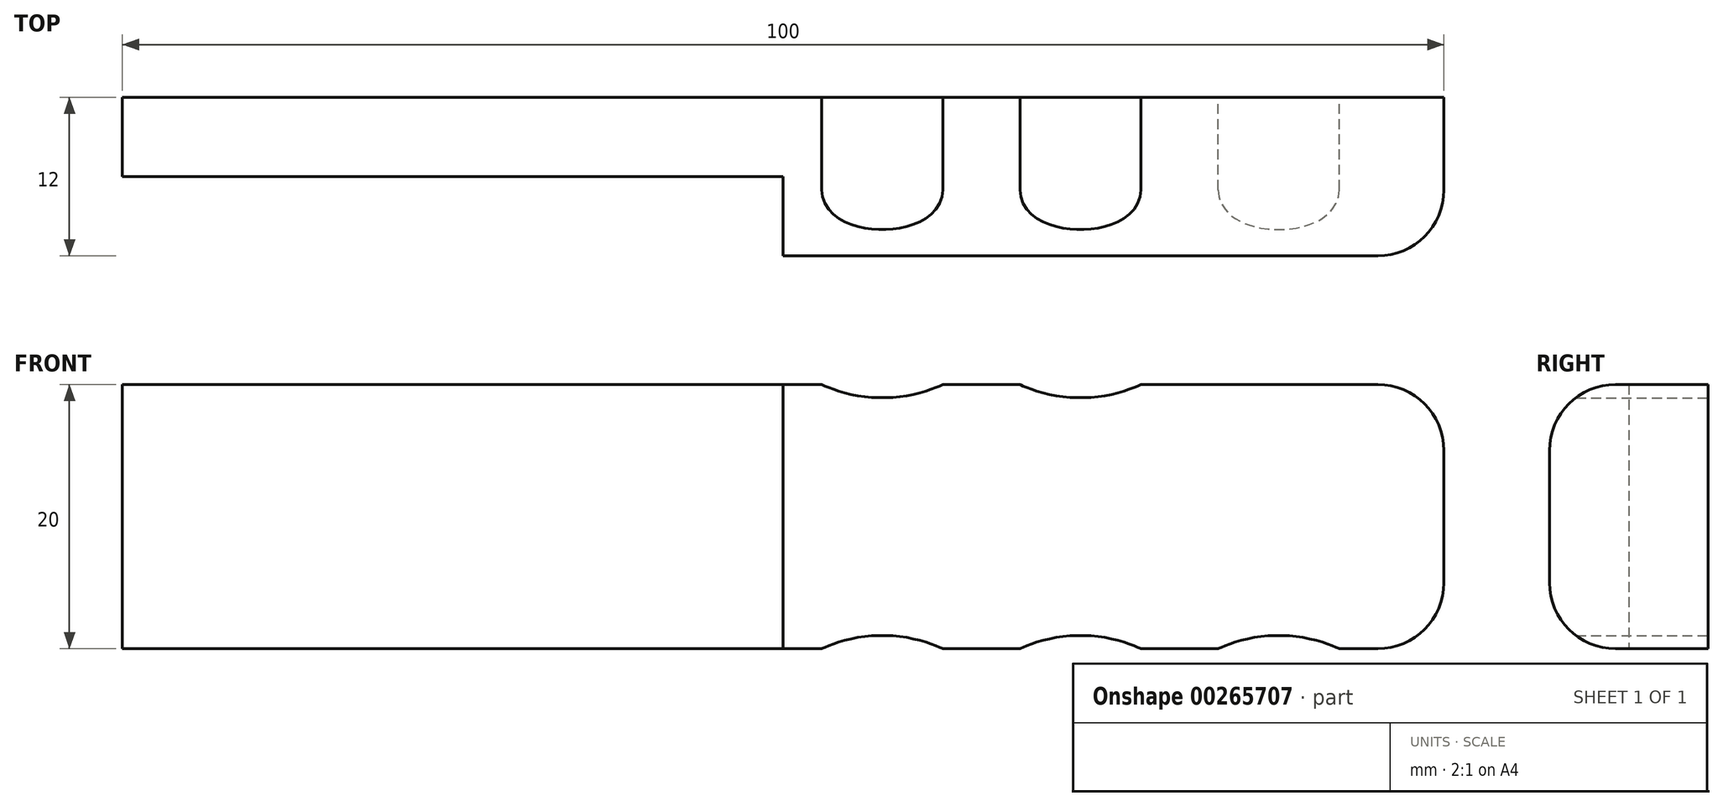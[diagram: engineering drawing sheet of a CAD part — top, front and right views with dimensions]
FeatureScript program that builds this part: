
annotation { "Feature Type Name" : "Feature", "Feature Type Description" : "" }
export const myFeature = defineFeature(function(context is Context, id is Id, definition is map)
    precondition{}
    {
        {
            var Q0;
            Q0=qCreatedBy(makeId("Front.planeOp"),FACE);
            var sketch = newSketch(context, id + "F0", { "sketchPlane" : qUnion([Q0])});
            skLineSegment(sketch, "E0.bottom", {"start": v(50, 10) * mm, "end": v(-50, 10) * mm});
            skLineSegment(sketch, "E0.top", {"start": v(50, -10) * mm, "end": v(-50, -10) * mm});
            skLineSegment(sketch, "E0.left", {"start": v(50, 10) * mm, "end": v(50, -10) * mm});
            skLineSegment(sketch, "E0.right", {"start": v(-50, 10) * mm, "end": v(-50, -10) * mm});
            skPoint(sketch, "E0.middle", {"position": v(0, 0) * mm});
            skSolve(sketch);
        }
        {
            var Q0;
            Q0=makeQuery(id+"F0.imprint","IMPRINT",FACE,{"disambiguationData":[TD([[makeQuery(id+"F0.imprint","IMPRINT",EDGE,{"derivedFrom":sQuery(id+"F0.wireOp",EDGE,"E0.bottom")}),1.0]])]});
            extrude(context, id + "F1", {"entities" : qUnion([Q0]), "depth" : 6 * mm});
        }
        {
            var Q0;
            Q0=makeQuery(id+"F1.opExtrude","SWEPT_EDGE",EDGE,{"disambiguationData":[OSD([sQuery(id+"F0.wireOp",EDGE,"E0.bottom"),sQuery(id+"F0.wireOp",EDGE,"E0.left")])]});
            var Q1;
            Q1=makeQuery(id+"F1.opExtrude","SWEPT_EDGE",EDGE,{"disambiguationData":[OSD([sQuery(id+"F0.wireOp",EDGE,"E0.top"),sQuery(id+"F0.wireOp",EDGE,"E0.left")])]});
            fillet(context, id + "F2", {"entities" : qUnion([Q0, Q1]), "radius" : 5 * mm, "tangentPropagation" : true, "allowEdgeOverflow" : false});
        }
        {
            var Q0;
            Q0=makeQuery(id+"F1.opExtrude","CAP_FACE",FACE,{"disambiguationData":[OSD([sQuery(id+"F0.wireOp",EDGE,"E0.bottom"),sQuery(id+"F0.wireOp",EDGE,"E0.top"),sQuery(id+"F0.wireOp",EDGE,"E0.left"),sQuery(id+"F0.wireOp",EDGE,"E0.right")])],"isStart":false});
            var sketch = newSketch(context, id + "F3", { "sketchPlane" : qUnion([Q0])});
            skLineSegment(sketch, "E1", {"start": v(0, 10) * mm, "end": v(0, -10) * mm});
            skSolve(sketch);
        }
        {
            var Q0;
            {var subQ6=sQuery(id+"F3.wireOp",EDGE,"E1");Q0=makeQuery(id+"F3.imprint","IMPRINT",FACE,{"disambiguationData":[TD([[makeQuery(id+"F3.imprint","IMPRINT",EDGE,{"derivedFrom":subQ6}),1.0]])]});}
            extrude(context, id + "F4", {"entities" : qUnion([Q0]), "operationType" : NewBodyOperationType.ADD, "depth" : 6 * mm});
        }
        {
            var Q0;
            Q0=makeQuery(id+"F4.opExtrude","CAP_EDGE",EDGE,{"disambiguationData":[OSD([sQuery(id+"F0.wireOp",EDGE,"E0.bottom")])],"isStart":false});
            fillet(context, id + "F5", {"entities" : qUnion([Q0]), "radius" : 5 * mm, "tangentPropagation" : true, "allowEdgeOverflow" : false});
        }
        {
            var Q0;
            Q0=qCreatedBy(makeId("Front.planeOp"),FACE);
            var sketch = newSketch(context, id + "F6", { "sketchPlane" : qUnion([Q0])});
            skLineSegment(sketch, "E2.0", {"start": v(0, 20) * mm, "end": v(45, 20) * mm});
            skCircle(sketch, "E3", {"center": v(7.5, 20) * mm, "radius": 11 * mm});
            skCircle(sketch, "E4.0.1.0", {"center": v(7.5, -20) * mm, "radius": 11 * mm});
            skCircle(sketch, "E4.1.0.0", {"center": v(22.5, 20) * mm, "radius": 11 * mm});
            skCircle(sketch, "E4.1.1.0", {"center": v(22.5, -20) * mm, "radius": 11 * mm});
            skCircle(sketch, "E4.2.0.0", {"center": v(37.5, 20) * mm, "radius": 11 * mm});
            skCircle(sketch, "E4.2.1.0", {"center": v(37.5, -20) * mm, "radius": 11 * mm});
            skLineSegment(sketch, "E4.direction1", {"start": v(7.5, 20) * mm, "end": v(22.5, 20) * mm, "construction": true});
            skLineSegment(sketch, "E4.direction2", {"start": v(7.5, 20) * mm, "end": v(7.5, -20) * mm, "construction": true});
            skSolve(sketch);
        }
        {
            var Q0;
            {var subQ0=sQuery(id+"F6.wireOp",EDGE,"E4.1.0.0");var subQ1=sQuery(id+"F6.wireOp",EDGE,"E3");var subQ2=makeQuery(id+"F6.imprint","INTERSECT",VERTEX,{"disambiguationData":[OD(0.0)],"derivedFrom":[subQ1,subQ0]});Q0=makeQuery(id+"F6.imprint","IMPRINT",FACE,{"disambiguationData":[TD([[makeQuery(id+"F6.imprint","IMPRINT",EDGE,{"disambiguationData":[TD([[subQ2,-1.0]])],"derivedFrom":subQ1}),1.0]])]});}
            var Q1;
            {var subQ0=sQuery(id+"F6.wireOp",EDGE,"E4.1.0.0");var subQ1=makeQuery(id+"F6.imprint","INTERSECT",VERTEX,{"disambiguationData":[OD(1.0)],"derivedFrom":[sQuery(id+"F6.wireOp",EDGE,"E2.0"),subQ0]});Q1=makeQuery(id+"F6.imprint","IMPRINT",FACE,{"disambiguationData":[TD([[makeQuery(id+"F6.imprint","IMPRINT",EDGE,{"disambiguationData":[TD([[subQ1,-1.0]])],"derivedFrom":subQ0}),-1.0]])]});}
            var Q2;
            {var subQ0=sQuery(id+"F6.wireOp",EDGE,"E3");var subQ1=sQuery(id+"F6.wireOp",EDGE,"E2.0");var subQ2=makeQuery(id+"F6.imprint","INTERSECT",VERTEX,{"derivedFrom":[subQ1,subQ0]});Q2=makeQuery(id+"F6.imprint","IMPRINT",FACE,{"disambiguationData":[TD([[makeQuery(id+"F6.imprint","IMPRINT",EDGE,{"disambiguationData":[TD([[subQ2,-1.0]])],"derivedFrom":subQ1}),-1.0]])]});}
            var Q3;
            {var subQ0=sQuery(id+"F6.wireOp",EDGE,"E4.1.1.0");var subQ1=sQuery(id+"F6.wireOp",EDGE,"E4.0.1.0");var subQ2=makeQuery(id+"F6.imprint","INTERSECT",VERTEX,{"disambiguationData":[OD(0.0)],"derivedFrom":[subQ1,subQ0]});Q3=makeQuery(id+"F6.imprint","IMPRINT",FACE,{"disambiguationData":[TD([[makeQuery(id+"F6.imprint","IMPRINT",EDGE,{"disambiguationData":[TD([[subQ2,-1.0]])],"derivedFrom":subQ1}),1.0]])]});}
            var Q4;
            {var subQ0=sQuery(id+"F6.wireOp",EDGE,"E4.1.1.0");var subQ1=sQuery(id+"F6.wireOp",EDGE,"E4.0.1.0");var subQ2=makeQuery(id+"F6.imprint","INTERSECT",VERTEX,{"disambiguationData":[OD(0.0)],"derivedFrom":[subQ1,subQ0]});Q4=makeQuery(id+"F6.imprint","IMPRINT",FACE,{"disambiguationData":[TD([[makeQuery(id+"F6.imprint","IMPRINT",EDGE,{"disambiguationData":[TD([[subQ2,1.0]])],"derivedFrom":subQ1}),-1.0]])]});}
            var Q5;
            {var subQ0=sQuery(id+"F6.wireOp",EDGE,"E4.2.1.0");var subQ1=sQuery(id+"F6.wireOp",EDGE,"E4.1.1.0");var subQ2=makeQuery(id+"F6.imprint","INTERSECT",VERTEX,{"disambiguationData":[OD(0.0)],"derivedFrom":[subQ1,subQ0]});Q5=makeQuery(id+"F6.imprint","IMPRINT",FACE,{"disambiguationData":[TD([[makeQuery(id+"F6.imprint","IMPRINT",EDGE,{"disambiguationData":[TD([[subQ2,1.0]])],"derivedFrom":subQ1}),-1.0]])]});}
            extrude(context, id + "F7", {"entities" : qUnion([Q0, Q1, Q2, Q3, Q4, Q5]), "operationType" : NewBodyOperationType.REMOVE, "depth" : 37 * mm});
        }
    });
